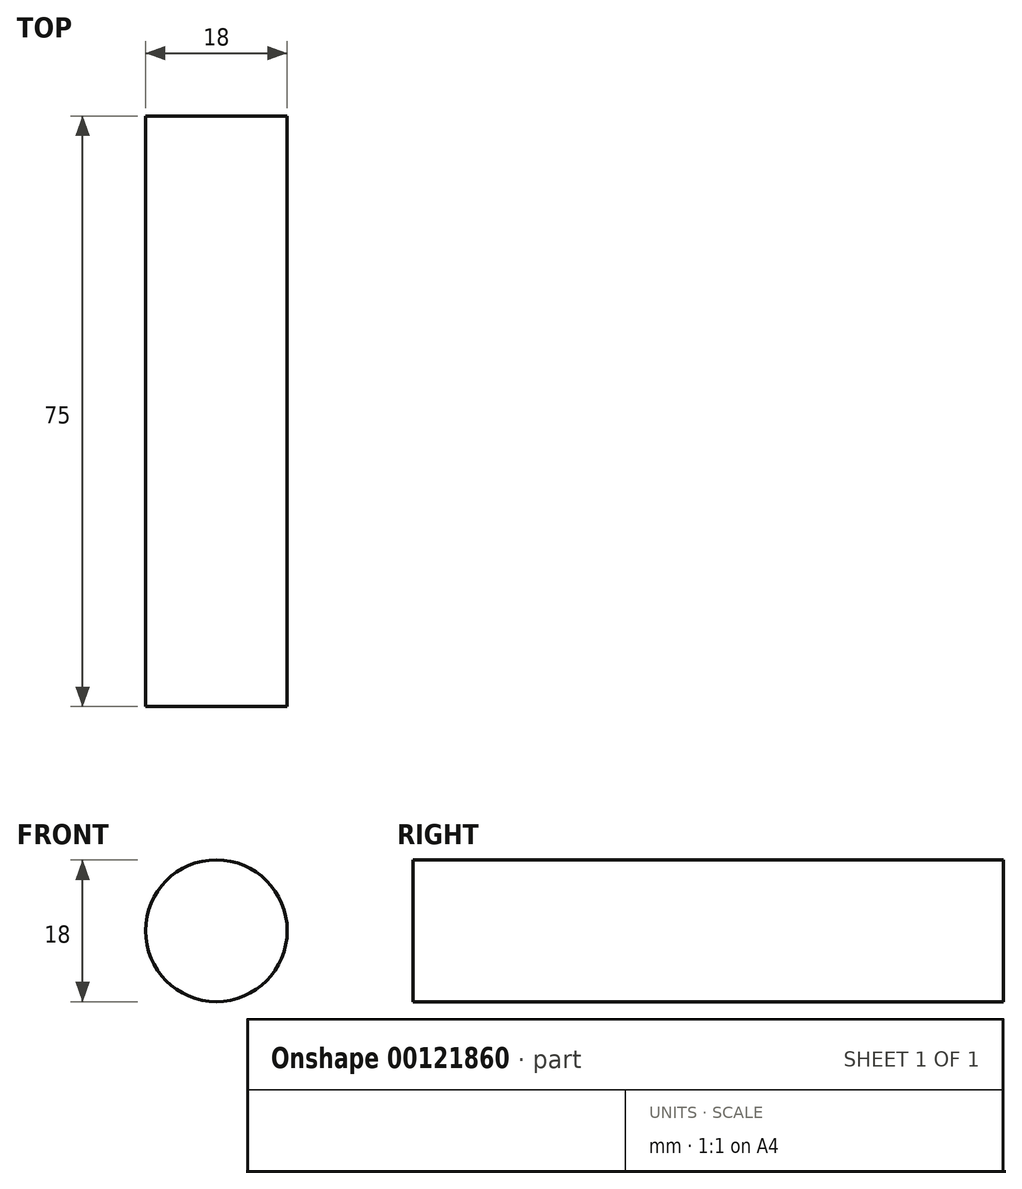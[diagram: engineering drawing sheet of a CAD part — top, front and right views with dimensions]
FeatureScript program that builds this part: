
annotation { "Feature Type Name" : "Feature", "Feature Type Description" : "" }
export const myFeature = defineFeature(function(context is Context, id is Id, definition is map)
    precondition{}
    {
        {
            var Q0;
            Q0=qCreatedBy(makeId("Front.planeOp"),FACE);
            var sketch = newSketch(context, id + "F0", { "sketchPlane" : qUnion([Q0])});
            skCircle(sketch, "E0", {"center": v(0, 0) * mm, "radius": 9 * mm});
            skSolve(sketch);
        }
        {
            var Q0;
            Q0 = qSketchRegion(id + "F0", true);
            extrude(context, id + "F1", {"entities" : qUnion([Q0]), "depth" : 75 * mm});
        }
    });
